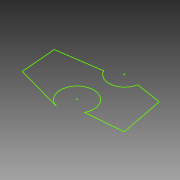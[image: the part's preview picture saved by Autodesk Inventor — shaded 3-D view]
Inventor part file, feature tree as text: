
AUTODESK INVENTOR PART (.ipt)
format: ipt  version: 2015 (Build 190159000, 159)  size: 59,904 bytes
history: native  units: mm
features: sketch x1
ambient origin geometry x8: Origin, YZ Plane, XZ Plane, XY Plane, X Axis, Y Axis, Z Axis, Center Point
feature tree (1):
  sketch  "Sketch1"
